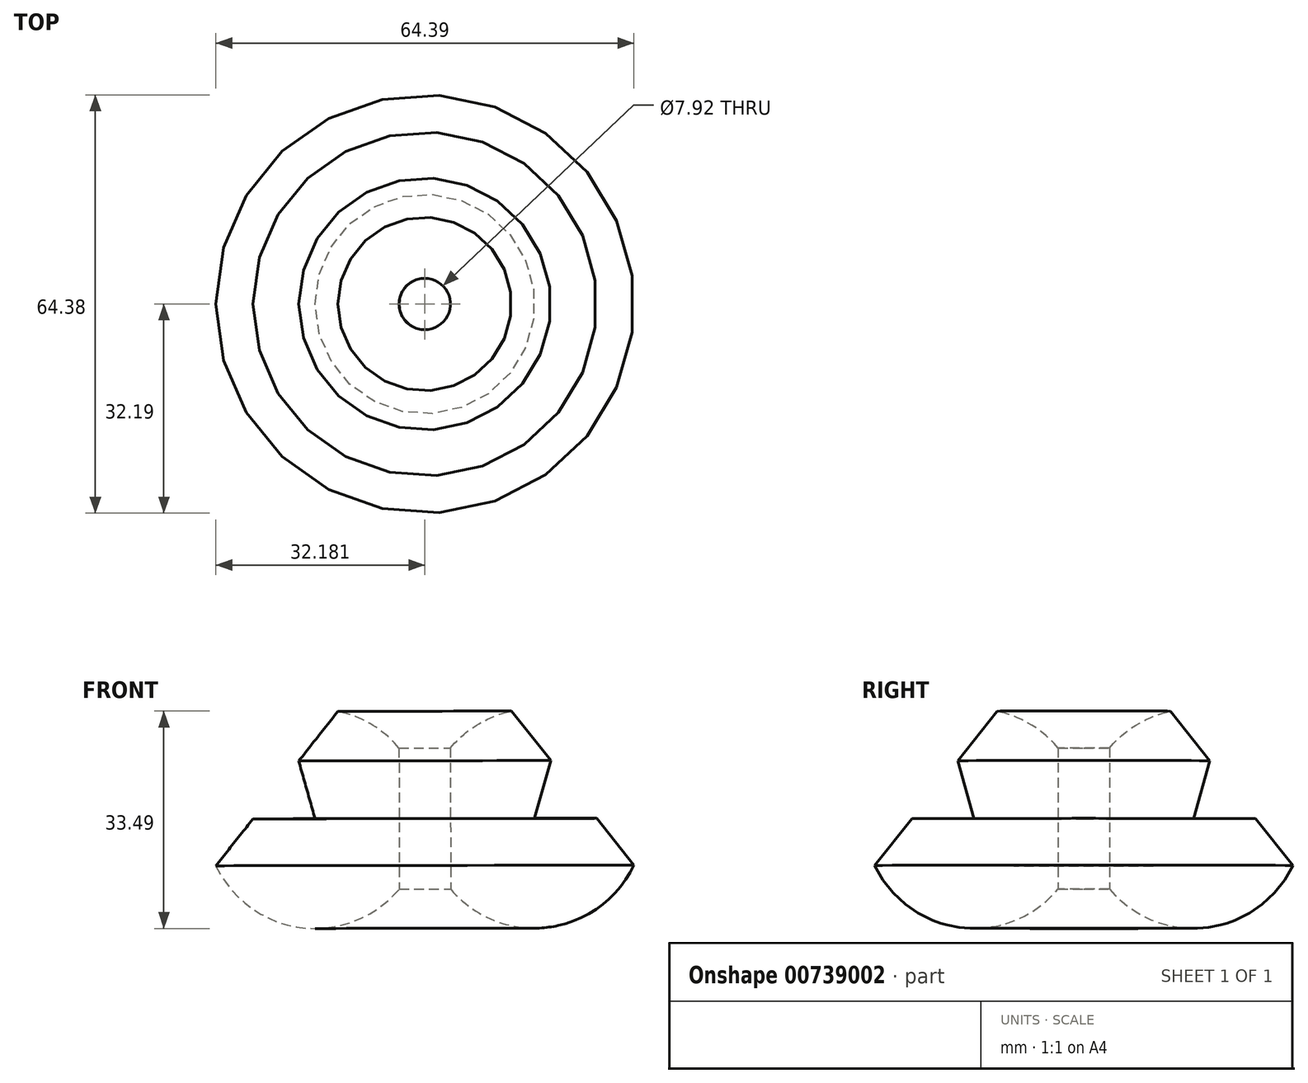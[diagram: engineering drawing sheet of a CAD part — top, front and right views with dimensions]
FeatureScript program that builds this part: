
annotation { "Feature Type Name" : "Feature", "Feature Type Description" : "" }
export const myFeature = defineFeature(function(context is Context, id is Id, definition is map)
    precondition{}
    {
        {
            var Q0;
            Q0=qCreatedBy(makeId("Front.planeOp"),FACE);
            var sketch = newSketch(context, id + "F0", { "sketchPlane" : qUnion([Q0])});
            skArc(sketch, "E0", {"start": v(13.3, 34.94) * mm, "mid": v(8.14, 32.88) * mm, "end": v(3.91, 29.27) * mm});
            skLineSegment(sketch, "E1", {"start": v(13.3, 34.94) * mm, "end": v(19.36, 27.32) * mm});
            skLineSegment(sketch, "E2", {"start": v(19.36, 27.32) * mm, "end": v(16.88, 18.41) * mm});
            skLineSegment(sketch, "E3", {"start": v(16.88, 18.41) * mm, "end": v(26.45, 18.41) * mm});
            skLineSegment(sketch, "E4.trimOffspring", {"start": v(26.45, 18.41) * mm, "end": v(32.18, 11.2) * mm});
            skLineSegment(sketch, "E5", {"start": v(0, 0) * mm, "end": v(-0.06, 37.72) * mm, "construction": true});
            skLineSegment(sketch, "E6", {"start": v(3.91, 29.27) * mm, "end": v(3.95, 7.52) * mm});
            skArc(sketch, "E7.trimOffspring", {"start": v(3.95, 7.52) * mm, "mid": v(19.07, 1.65) * mm, "end": v(32.18, 11.2) * mm});
            skSolve(sketch);
        }
        {
            var Q0;
            Q0=makeQuery(id+"F0.imprint","IMPRINT",FACE,{"disambiguationData":[TD([[makeQuery(id+"F0.imprint","IMPRINT",EDGE,{"derivedFrom":sQuery(id+"F0.wireOp",EDGE,"E0")}),1.0]])]});
            var Q1;
            Q1=sQuery(id+"F0.wireOp",EDGE,"E5");
            revolve(context, id + "F1", {"surfaceOperationType" : NewSurfaceOperationType.NEW, "entities" : qUnion([Q0]), "axis" : qUnion([Q1]), "revolveType" : RevolveType.FULL});
        }
    });
